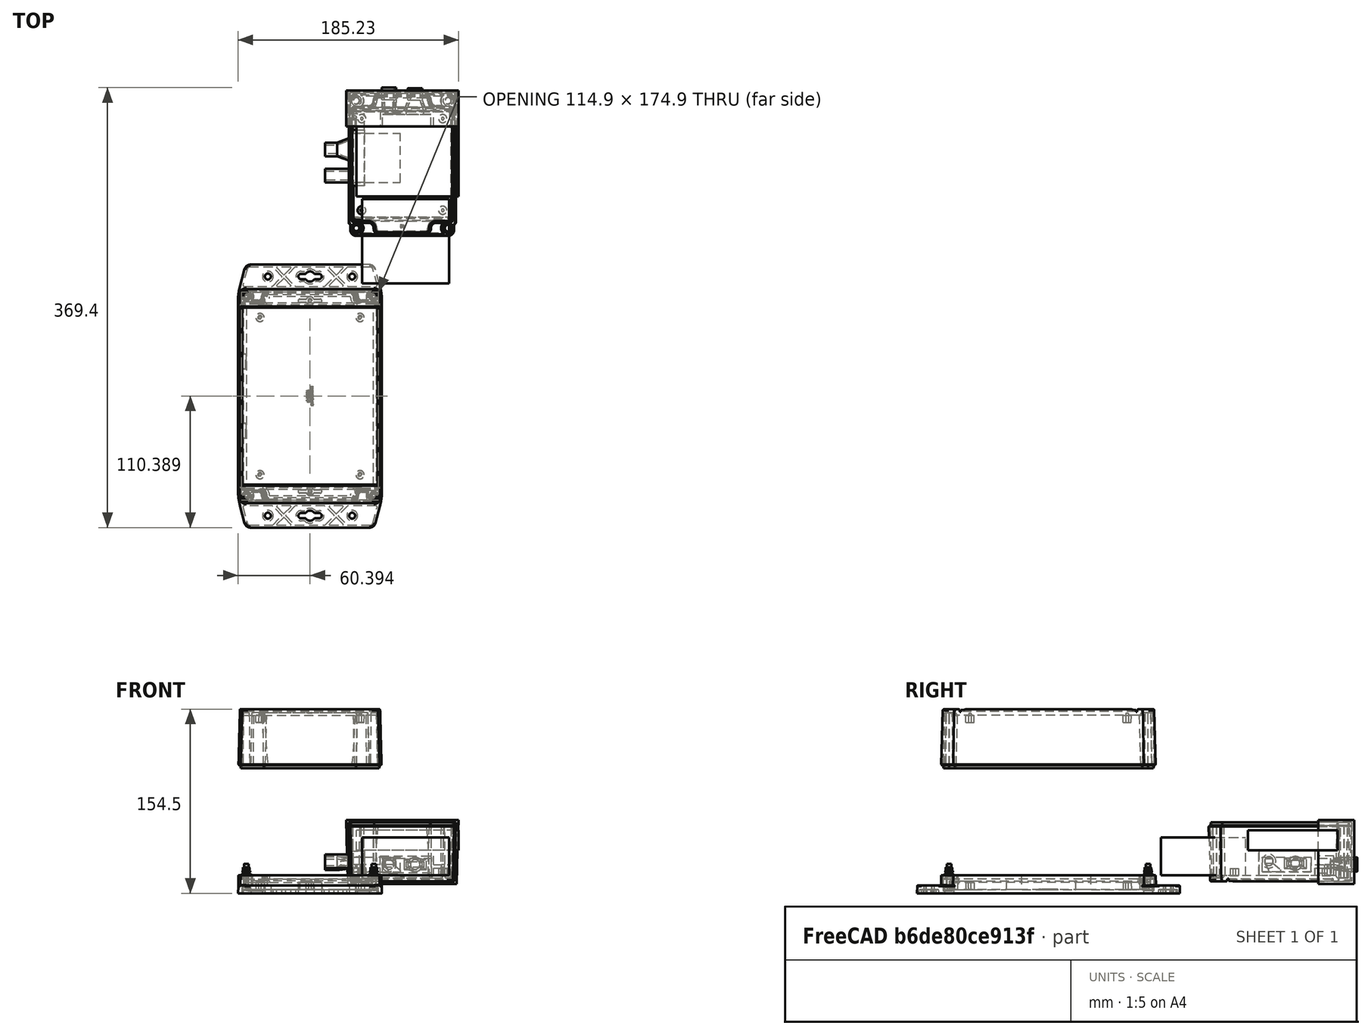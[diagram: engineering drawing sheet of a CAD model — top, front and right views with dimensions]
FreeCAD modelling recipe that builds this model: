
FCSTD DOCUMENT  (FreeCAD 0.19R24366 (Git))
Label: pzld_pm_sensor_mount
License: All rights reserved
LicenseURL: http://en.wikipedia.org/wiki/All_rights_reserved
objects: Sketcher::SketchObject×25, Part::Feature×12, PartDesign::Pad×11, PartDesign::Pocket×10, PartDesign::AdditiveLoft×3, PartDesign::Body×3, Part::Box×3, App::Part×2, PartDesign::ShapeBinder×2, TechDraw::DrawSVGTemplate×1, TechDraw::DrawViewPart×1, TechDraw::DrawViewDimension×1, TechDraw::DrawPage×1, Spreadsheet::Sheet×1
note: 93 computed .brp shape members not serialized (recipe doc carries the construction recipe); baked Part::Feature solids carry a one-line shape summary decoded from their .brp

FEATURE [Sketcher::SketchObject] Sketch  label="ref"
  FullyConstrained = false
  sketch-geometry (40):
    g0: LineSegment StartX=110.922 StartY=9.52227 StartZ=0 EndX=100.422 EndY=9.52227 EndZ=0
    g1: ArcOfCircle CenterX=110.922 CenterY=12.5223 CenterZ=0 NormalX=0 NormalY=0 NormalZ=1 AngleXU=0 Radius=3 StartAngle=4.71239 EndAngle=6.28319
    g2: LineSegment StartX=113.922 StartY=161.522 StartZ=0 EndX=113.922 EndY=12.5223 EndZ=0
    g3: ArcOfCircle CenterX=110.922 CenterY=161.522 CenterZ=0 NormalX=0 NormalY=0 NormalZ=1 AngleXU=0 Radius=3 StartAngle=0 EndAngle=1.5708
    g4: LineSegment StartX=100.422 StartY=164.522 StartZ=0 EndX=110.922 EndY=164.522 EndZ=0
    g5: LineSegment StartX=94.4224 StartY=171.022 StartZ=0 EndX=94.4224 EndY=170.522 EndZ=0
    g6: ArcOfCircle CenterX=91.4224 CenterY=171.022 CenterZ=0 NormalX=0 NormalY=0 NormalZ=1 AngleXU=0 Radius=3 StartAngle=0 EndAngle=1.5708
    g7: LineSegment StartX=22.4224 StartY=174.022 StartZ=0 EndX=91.4224 EndY=174.022 EndZ=0
    g8: ArcOfCircle CenterX=22.4224 CenterY=171.022 CenterZ=0 NormalX=0 NormalY=0 NormalZ=1 AngleXU=0 Radius=3 StartAngle=1.5708 EndAngle=3.14159
    g9: LineSegment StartX=19.4224 StartY=170.522 StartZ=0 EndX=19.4224 EndY=171.022 EndZ=0
    g10: ArcOfCircle CenterX=13.4224 CenterY=170.522 CenterZ=0 NormalX=0 NormalY=0 NormalZ=1 AngleXU=0 Radius=6 StartAngle=4.71239 EndAngle=6.28319
    g11: ArcOfCircle CenterX=100.422 CenterY=170.522 CenterZ=0 NormalX=0 NormalY=0 NormalZ=1 AngleXU=0 Radius=6 StartAngle=3.14159 EndAngle=4.71239
    g12: LineSegment StartX=2.92236 StartY=164.522 StartZ=0 EndX=13.4224 EndY=164.522 EndZ=0
    g13: ArcOfCircle CenterX=2.92236 CenterY=161.522 CenterZ=0 NormalX=0 NormalY=0 NormalZ=1 AngleXU=0 Radius=3 StartAngle=1.5708 EndAngle=3.14159
    g14: LineSegment StartX=-0.0776441 StartY=12.5223 StartZ=0 EndX=-0.0776441 EndY=161.522 EndZ=0
    g15: ArcOfCircle CenterX=2.92236 CenterY=12.5223 CenterZ=0 NormalX=0 NormalY=0 NormalZ=1 AngleXU=0 Radius=3 StartAngle=3.14159 EndAngle=4.71239
    g16: LineSegment StartX=13.4224 StartY=9.52227 StartZ=0 EndX=2.92236 EndY=9.52227 EndZ=0
    g17: ArcOfCircle CenterX=13.4224 CenterY=3.52227 CenterZ=0 NormalX=0 NormalY=0 NormalZ=1 AngleXU=0 Radius=6 StartAngle=0 EndAngle=1.5708
    g18: LineSegment StartX=19.4224 StartY=3.02227 StartZ=0 EndX=19.4224 EndY=3.52227 EndZ=0
    g19: ArcOfCircle CenterX=22.4224 CenterY=3.02227 CenterZ=0 NormalX=0 NormalY=0 NormalZ=1 AngleXU=0 Radius=3 StartAngle=3.14159 EndAngle=4.71239
    g20: LineSegment StartX=91.4224 StartY=0.0222689 StartZ=0 EndX=22.4224 EndY=0.0222689 EndZ=0
    g21: ArcOfCircle CenterX=91.4224 CenterY=3.02227 CenterZ=0 NormalX=0 NormalY=0 NormalZ=1 AngleXU=0 Radius=3 StartAngle=4.71239 EndAngle=6.28319
    g22: LineSegment StartX=94.4224 StartY=3.52227 StartZ=0 EndX=94.4224 EndY=3.02227 EndZ=0
    g23: ArcOfCircle CenterX=100.422 CenterY=3.52227 CenterZ=0 NormalX=0 NormalY=0 NormalZ=1 AngleXU=0 Radius=6 StartAngle=1.5708 EndAngle=3.14159
    g24: Circle CenterX=14.9224 CenterY=153.022 CenterZ=0 NormalX=0 NormalY=0 NormalZ=-1 AngleXU=0 Radius=1.05955
    g25: Circle CenterX=14.9224 CenterY=153.022 CenterZ=0 NormalX=0 NormalY=0 NormalZ=-1 AngleXU=0 Radius=1.125
    g26: Circle CenterX=14.9224 CenterY=153.022 CenterZ=0 NormalX=0 NormalY=0 NormalZ=-1 AngleXU=0 Radius=3.39527
    g27: Circle CenterX=98.9224 CenterY=153.022 CenterZ=0 NormalX=0 NormalY=0 NormalZ=-1 AngleXU=0 Radius=3.39527
    g28: Circle CenterX=14.9224 CenterY=21.0223 CenterZ=0 NormalX=0 NormalY=0 NormalZ=-1 AngleXU=0 Radius=3.39527
    g29: Circle CenterX=98.9224 CenterY=21.0223 CenterZ=0 NormalX=0 NormalY=0 NormalZ=-1 AngleXU=0 Radius=3.39527
    g30: Circle CenterX=98.9224 CenterY=21.0223 CenterZ=0 NormalX=0 NormalY=0 NormalZ=-1 AngleXU=0 Radius=3.5
    g31: Circle CenterX=14.9224 CenterY=21.0223 CenterZ=0 NormalX=0 NormalY=0 NormalZ=-1 AngleXU=0 Radius=3.5
    g32: Circle CenterX=14.9224 CenterY=153.022 CenterZ=0 NormalX=0 NormalY=0 NormalZ=-1 AngleXU=0 Radius=3.5
    g33: Circle CenterX=98.9224 CenterY=153.022 CenterZ=0 NormalX=0 NormalY=0 NormalZ=-1 AngleXU=0 Radius=3.5
    g34: Circle CenterX=98.9224 CenterY=153.022 CenterZ=0 NormalX=0 NormalY=0 NormalZ=-1 AngleXU=0 Radius=1.05955
    g35: Circle CenterX=98.9224 CenterY=153.022 CenterZ=0 NormalX=0 NormalY=0 NormalZ=-1 AngleXU=0 Radius=1.125
    g36: Circle CenterX=14.9224 CenterY=21.0223 CenterZ=0 NormalX=0 NormalY=0 NormalZ=-1 AngleXU=0 Radius=1.05955
    g37: Circle CenterX=14.9224 CenterY=21.0223 CenterZ=0 NormalX=0 NormalY=0 NormalZ=-1 AngleXU=0 Radius=1.125
    g38: Circle CenterX=98.9224 CenterY=21.0223 CenterZ=0 NormalX=0 NormalY=0 NormalZ=-1 AngleXU=0 Radius=1.05955
    g39: Circle CenterX=98.9224 CenterY=21.0223 CenterZ=0 NormalX=0 NormalY=0 NormalZ=-1 AngleXU=0 Radius=1.125
  constraints (2):
    c: Radius(g32) = 3.5
    c: Radius(g25) = 1.125
FEATURE [Sketcher::SketchObject] Sketch001  label="base"
  ExternalGeometry = -> [Sketch]
  FullyConstrained = true
  MapMode = 5
  Support = -> [XY_Plane]
  sketch-geometry (9):
    g0: LineSegment StartX=12.9224 StartY=140.022 StartZ=0 EndX=53.9224 EndY=140.022 EndZ=0
    g1: LineSegment StartX=53.9224 StartY=140.022 StartZ=0 EndX=53.9224 EndY=99.0223 EndZ=0
    g2: LineSegment StartX=53.9224 StartY=99.0223 StartZ=0 EndX=12.9224 EndY=99.0223 EndZ=0
    g3: LineSegment StartX=12.9224 StartY=99.0223 StartZ=0 EndX=12.9224 EndY=140.022 EndZ=0
    g4: LineSegment StartX=9.92236 StartY=143.022 StartZ=0 EndX=68.9224 EndY=143.022 EndZ=0
    g5: LineSegment StartX=68.9224 StartY=143.022 StartZ=0 EndX=68.9224 EndY=96.0223 EndZ=0
    g6: LineSegment StartX=68.9224 StartY=96.0223 StartZ=0 EndX=9.92236 EndY=96.0223 EndZ=0
    g7: LineSegment StartX=9.92236 StartY=96.0223 StartZ=0 EndX=9.92236 EndY=143.022 EndZ=0
    g8: GeomPoint X=-0.0776441 Y=96.0223 Z=0
  constraints (26):
    c: Coincident(g0,g1)
    c: Coincident(g1,g2)
    c: Coincident(g2,g3)
    c: Coincident(g3,g0)
    c: Horizontal(g0)
    c: Horizontal(g2)
    c: Vertical(g1)
    c: Vertical(g3)
    c: DistanceX(g0,g0) = 41
    c: DistanceY(g1,g1) = 41
    c: Coincident(g4,g5)
    c: Coincident(g5,g6)
    c: Coincident(g6,g7)
    c: Coincident(g7,g4)
    c: Horizontal(g4)
    c: Horizontal(g6)
    c: Vertical(g5)
    c: Vertical(g7)
    c: DistanceX(g4,g0) = 3
    c: DistanceY(g0,g4) = 3
    c: DistanceX(g0,g4) = 15
    c: DistanceY(g5,g1) = 3
    c: PointOnObject(g8,g-3)
    c: Horizontal(g8,g6)
    c: DistanceX(g8,g6) = 10
    c: DistanceY(g4,g-4) = 10
FEATURE [PartDesign::Pad] Pad
  Direction = (1,1,1)
  Length = 20.5
  Length2 = 100
  Profile = -> Sketch001
  Type = 0
FEATURE [Sketcher::SketchObject] Sketch002
  ExternalGeometry = -> [Pad]
  FullyConstrained = true
  MapMode = 5
  Placement = pos=(0,0,20.5) rot=(0,0,1;0rad)
  Support = -> [Pad]
  sketch-geometry (4):
    g0: LineSegment StartX=68.9224 StartY=143.022 StartZ=0 EndX=22.9224 EndY=143.022 EndZ=0
    g1: LineSegment StartX=22.9224 StartY=143.022 StartZ=0 EndX=22.9224 EndY=96.0223 EndZ=0
    g2: LineSegment StartX=22.9224 StartY=96.0223 StartZ=0 EndX=68.9224 EndY=96.0223 EndZ=0
    g3: LineSegment StartX=68.9224 StartY=96.0223 StartZ=0 EndX=68.9224 EndY=143.022 EndZ=0
  constraints (11):
    c: Coincident(g0,g1)
    c: Coincident(g1,g2)
    c: Coincident(g2,g3)
    c: Coincident(g3,g0)
    c: Horizontal(g0)
    c: Horizontal(g2)
    c: Vertical(g1)
    c: Vertical(g3)
    c: Coincident(g0,g-5)
    c: PointOnObject(g1,g-4)
    c: DistanceX(g-6,g0) = 13
FEATURE [PartDesign::Pocket] Pocket
  BaseFeature = -> Pad
  Length = 17.5
  Length2 = 100
  Profile = -> Sketch002
  Type = 0
FEATURE [Sketcher::SketchObject] Sketch003
  ExternalGeometry = -> [Pocket]
  FullyConstrained = true
  MapMode = 5
  Placement = pos=(22.9224,0,0) rot=(0.57735,0.57735,0.57735;2.0944rad)
  Support = -> [Pocket]
  sketch-geometry (4):
    g0: LineSegment StartX=99.0223 StartY=15.5 StartZ=0 EndX=140.022 EndY=15.5 EndZ=0
    g1: LineSegment StartX=140.022 StartY=15.5 StartZ=0 EndX=140.022 EndY=3 EndZ=0
    g2: LineSegment StartX=140.022 StartY=3 StartZ=0 EndX=99.0223 EndY=3 EndZ=0
    g3: LineSegment StartX=99.0223 StartY=3 StartZ=0 EndX=99.0223 EndY=15.5 EndZ=0
  constraints (12):
    c: Coincident(g0,g1)
    c: Coincident(g1,g2)
    c: Coincident(g2,g3)
    c: Coincident(g3,g0)
    c: Horizontal(g0)
    c: Horizontal(g2)
    c: Vertical(g1)
    c: Vertical(g3)
    c: DistanceX(g-4,g0) = 3
    c: DistanceX(g0,g-5) = 3
    c: PointOnObject(g1,g-6)
    c: DistanceY(g3,g3) = 12.5
FEATURE [PartDesign::Pocket] Pocket001
  BaseFeature = -> Pocket
  Length = 10
  Length2 = 100
  Profile = -> Sketch003
  Type = 0
FEATURE [Sketcher::SketchObject] Sketch004
  ExternalGeometry = -> [Pocket001]
  FullyConstrained = true
  MapMode = 5
  Placement = pos=(9.92236,0,0) rot=(0.57735,-0.57735,-0.57735;2.0944rad)
  Support = -> [Pocket001]
  sketch-geometry (11):
    g0: LineSegment StartX=-143.022 StartY=3 StartZ=0 EndX=-96.0223 EndY=3 EndZ=0
    g1: LineSegment StartX=-134.022 StartY=12.55 StartZ=0 EndX=-119.222 EndY=12.55 EndZ=0
    g2: LineSegment StartX=-119.222 StartY=12.55 StartZ=0 EndX=-119.222 EndY=7.8 EndZ=0
    g3: LineSegment StartX=-119.222 StartY=7.8 StartZ=0 EndX=-134.022 EndY=7.8 EndZ=0
    g4: LineSegment StartX=-134.022 StartY=7.8 StartZ=0 EndX=-134.022 EndY=12.55 EndZ=0
    g5: LineSegment StartX=-107.822 StartY=13.7 StartZ=0 EndX=-101.222 EndY=13.7 EndZ=0
    g6: LineSegment StartX=-101.222 StartY=13.7 StartZ=0 EndX=-101.222 EndY=10.2 EndZ=0
    g7: LineSegment StartX=-101.222 StartY=10.2 StartZ=0 EndX=-107.822 EndY=10.2 EndZ=0
    g8: LineSegment StartX=-107.822 StartY=10.2 StartZ=0 EndX=-107.822 EndY=13.7 EndZ=0
    g9: LineSegment StartX=-140.022 StartY=20.5 StartZ=0 EndX=-140.022 EndY=3 EndZ=0
    g10: LineSegment StartX=-99.0223 StartY=20.5 StartZ=0 EndX=-99.0223 EndY=3 EndZ=0
  constraints (36):
    c: PointOnObject(g0,g-5)
    c: PointOnObject(g0,g-4)
    c: Horizontal(g0)
    c: DistanceY(g-6,g0) = 3
    c: Coincident(g1,g2)
    c: Coincident(g2,g3)
    c: Coincident(g3,g4)
    c: Coincident(g4,g1)
    c: Horizontal(g1)
    c: Horizontal(g3)
    c: Vertical(g2)
    c: Vertical(g4)
    c: DistanceY(g0,g3) = 4.8
    c: DistanceX(g1,g1) = 14.8
    c: DistanceY(g4,g4) = 4.75
    c: Coincident(g5,g6)
    c: Coincident(g6,g7)
    c: Coincident(g7,g8)
    c: Coincident(g8,g5)
    c: Horizontal(g5)
    c: Horizontal(g7)
    c: Vertical(g6)
    c: Vertical(g8)
    c: DistanceX(g5,g5) = 6.6
    c: DistanceY(g8,g8) = 3.5
    c: PointOnObject(g9,g-3)
    c: PointOnObject(g9,g0)
    c: Vertical(g9)
    c: PointOnObject(g10,g-3)
    c: PointOnObject(g10,g0)
    c: Vertical(g10)
    c: DistanceX(g-5,g9) = 3
    c: DistanceX(g10,g-4) = 3
    c: DistanceX(g9,g1) = 6
    c: DistanceX(g5,g10) = 2.2
    c: DistanceY(g0,g6) = 7.2
FEATURE [PartDesign::Pocket] Pocket002
  BaseFeature = -> Pocket001
  Length = 5
  Length2 = 100
  Profile = -> Sketch004
  Type = 0
FEATURE [Sketcher::SketchObject] Sketch005
  ExternalGeometry = -> [Pocket002]
  FullyConstrained = true
  MapMode = 5
  Placement = pos=(12.9224,0,0) rot=(0.57735,0.57735,0.57735;2.0944rad)
  Support = -> [Pocket002]
  sketch-geometry (7):
    g0: LineSegment StartX=104.222 StartY=5 StartZ=0 EndX=114.222 EndY=5 EndZ=0
    g1: LineSegment StartX=114.222 StartY=5 StartZ=0 EndX=114.222 EndY=3 EndZ=0
    g2: LineSegment StartX=114.222 StartY=3 StartZ=0 EndX=104.222 EndY=3 EndZ=0
    g3: LineSegment StartX=104.222 StartY=3 StartZ=0 EndX=104.222 EndY=5 EndZ=0
    g4: LineSegment StartX=107.822 StartY=10.2 StartZ=0 EndX=114.222 EndY=5 EndZ=0
    g5: LineSegment StartX=104.222 StartY=5 StartZ=0 EndX=101.222 EndY=10.2 EndZ=0
    g6: LineSegment StartX=101.222 StartY=10.2 StartZ=0 EndX=107.822 EndY=10.2 EndZ=0
  constraints (18):
    c: Coincident(g0,g1)
    c: Coincident(g1,g2)
    c: Coincident(g2,g3)
    c: Coincident(g3,g0)
    c: Horizontal(g0)
    c: Horizontal(g2)
    c: Vertical(g1)
    c: Vertical(g3)
    c: DistanceX(g0,g0) = 10
    c: DistanceY(g1,g1) = 2
    c: DistanceX(g-4,g2) = 5.2
    c: PointOnObject(g2,g-5)
    c: Coincident(g4,g-3)
    c: Coincident(g4,g0)
    c: Coincident(g5,g0)
    c: Coincident(g5,g-3)
    c: Coincident(g6,g5)
    c: Coincident(g6,g4)
FEATURE [PartDesign::Pocket] Pocket003
  BaseFeature = -> Pocket002
  Length = 1.5
  Length2 = 100
  Profile = -> Sketch005
  Type = 0
FEATURE [Sketcher::SketchObject] Sketch006
  ExternalGeometry = -> [Pocket003]
  FullyConstrained = true
  MapMode = 5
  Placement = pos=(9.92236,0,0) rot=(0.57735,-0.57735,-0.57735;2.0944rad)
  Support = -> [Pocket003]
  sketch-geometry (6):
    g0: LineSegment StartX=-107.822 StartY=10.2 StartZ=0 EndX=-101.222 EndY=13.7 EndZ=0
    g1: LineSegment StartX=-107.822 StartY=13.7 StartZ=0 EndX=-101.222 EndY=10.2 EndZ=0
    g2: GeomPoint X=-104.522 Y=11.95 Z=0
    g3: Circle CenterX=-104.522 CenterY=11.95 CenterZ=0 NormalX=0 NormalY=0 NormalZ=1 AngleXU=0 Radius=3.7353
    g4: Circle CenterX=-104.522 CenterY=11.95 CenterZ=0 NormalX=0 NormalY=0 NormalZ=1 AngleXU=0 Radius=5.7353
    g5: LineSegment StartX=-100.787 StartY=11.95 StartZ=0 EndX=-98.787 EndY=11.95 EndZ=0
  constraints (14):
    c: Coincident(g0,g-3)
    c: Coincident(g0,g-5)
    c: Coincident(g1,g-4)
    c: Coincident(g1,g-6)
    c: PointOnObject(g2,g0)
    c: PointOnObject(g2,g1)
    c: Coincident(g3,g2)
    c: PointOnObject(g0,g3)
    c: Coincident(g4,g3)
    c: PointOnObject(g5,g3)
    c: PointOnObject(g5,g4)
    c: Horizontal(g5)
    c: Perpendicular(g3,g5)
    c: DistanceX(g5,g5) = 2
FEATURE [PartDesign::Pad] Pad001
  BaseFeature = -> Pocket003
  Direction = (1,1,1)
  Length = 20
  Length2 = 100
  Profile = -> Sketch006
  Type = 0
FEATURE [Sketcher::SketchObject] Sketch007
  ExternalGeometry = -> [Pad001]
  FullyConstrained = true
  MapMode = 5
  Placement = pos=(9.92236,0,0) rot=(0.57735,-0.57735,-0.57735;2.0944rad)
  Support = -> [Pad001]
  sketch-geometry (8):
    g0: LineSegment StartX=-134.022 StartY=12.55 StartZ=0 EndX=-119.222 EndY=12.55 EndZ=0
    g1: LineSegment StartX=-119.222 StartY=12.55 StartZ=0 EndX=-119.222 EndY=7.8 EndZ=0
    g2: LineSegment StartX=-119.222 StartY=7.8 StartZ=0 EndX=-134.022 EndY=7.8 EndZ=0
    g3: LineSegment StartX=-134.022 StartY=7.8 StartZ=0 EndX=-134.022 EndY=12.55 EndZ=0
    g4: LineSegment StartX=-136.022 StartY=14.55 StartZ=0 EndX=-117.222 EndY=14.55 EndZ=0
    g5: LineSegment StartX=-117.222 StartY=14.55 StartZ=0 EndX=-117.222 EndY=5.8 EndZ=0
    g6: LineSegment StartX=-117.222 StartY=5.8 StartZ=0 EndX=-136.022 EndY=5.8 EndZ=0
    g7: LineSegment StartX=-136.022 StartY=5.8 StartZ=0 EndX=-136.022 EndY=14.55 EndZ=0
  constraints (22):
    c: Coincident(g0,g1)
    c: Coincident(g1,g2)
    c: Coincident(g2,g3)
    c: Coincident(g3,g0)
    c: Horizontal(g0)
    c: Horizontal(g2)
    c: Vertical(g1)
    c: Vertical(g3)
    c: Coincident(g0,g-3)
    c: Coincident(g1,g-4)
    c: Coincident(g4,g5)
    c: Coincident(g5,g6)
    c: Coincident(g6,g7)
    c: Coincident(g7,g4)
    c: Horizontal(g4)
    c: Horizontal(g6)
    c: Vertical(g5)
    c: Vertical(g7)
    c: DistanceY(g0,g4) = 2
    c: DistanceX(g4,g0) = 2
    c: DistanceX(g1,g5) = 2
    c: DistanceY(g5,g1) = 2
FEATURE [Sketcher::SketchObject] Sketch008
  AttachmentOffset = pos=(0,7,10) rot=(0,0,1;0rad)
  ExternalGeometry = -> [Pad001]
  FullyConstrained = true
  MapMode = 5
  Placement = pos=(-0.0776441,0,7) rot=(0.57735,-0.57735,-0.57735;2.0944rad)
  Support = -> [Pad001]
  sketch-geometry (6):
    g0: LineSegment StartX=-134.022 StartY=5.55 StartZ=0 EndX=-119.222 EndY=0.8 EndZ=0
    g1: LineSegment StartX=-119.222 StartY=5.55 StartZ=0 EndX=-134.022 EndY=0.8 EndZ=0
    g2: GeomPoint X=-126.622 Y=3.175 Z=0
    g3: Circle CenterX=-126.622 CenterY=3.175 CenterZ=0 NormalX=0 NormalY=0 NormalZ=1 AngleXU=0 Radius=3.73
    g4: Circle CenterX=-126.622 CenterY=3.175 CenterZ=0 NormalX=0 NormalY=0 NormalZ=1 AngleXU=0 Radius=5.73
    g5: LineSegment StartX=-122.892 StartY=3.175 StartZ=0 EndX=-120.892 EndY=3.175 EndZ=0
  constraints (14):
    c: Coincident(g0,g-3)
    c: Coincident(g0,g-4)
    c: Coincident(g1,g-5)
    c: Coincident(g1,g-6)
    c: PointOnObject(g2,g1)
    c: PointOnObject(g2,g0)
    c: Coincident(g3,g2)
    c: Coincident(g4,g3)
    c: PointOnObject(g5,g3)
    c: PointOnObject(g5,g4)
    c: Horizontal(g5)
    c: Perpendicular(g3,g5)
    c: DistanceX(g5,g5) = 2
    c: Radius(g3) = 3.73
FEATURE [PartDesign::AdditiveLoft] AdditiveLoft
  BaseFeature = -> Pad001
  Closed = false
  Profile = -> Sketch007
  Ruled = false
  Sections = -> [Sketch008]
FEATURE [PartDesign::Pad] Pad002
  BaseFeature = -> AdditiveLoft
  Direction = (1,1,1)
  Length = 10
  Length2 = 100
  Profile = -> AdditiveLoft [Face22]
  Type = 0
FEATURE [Sketcher::SketchObject] Sketch009
  ExternalGeometry = -> [Pad002]
  FullyConstrained = true
  MapMode = 5
  Placement = pos=(0,143.022,0) rot=(0,0.707107,0.707107;3.14159rad)
  Support = -> [Pad002]
  sketch-geometry (5):
    g0: GeomPoint X=-9.92236 Y=6 Z=0
    g1: LineSegment StartX=-9.92236 StartY=6 StartZ=0 EndX=-22.9224 EndY=6 EndZ=0
    g2: LineSegment StartX=-22.9224 StartY=6 StartZ=0 EndX=-22.9224 EndY=9 EndZ=0
    g3: LineSegment StartX=-22.9224 StartY=9 StartZ=0 EndX=-9.92236 EndY=9 EndZ=0
    g4: LineSegment StartX=-9.92236 StartY=9 StartZ=0 EndX=-9.92236 EndY=6 EndZ=0
  constraints (13):
    c: PointOnObject(g0,g-4)
    c: DistanceY(g-4,g0) = 6
    c: Coincident(g1,g2)
    c: Coincident(g2,g3)
    c: Coincident(g3,g4)
    c: Coincident(g4,g1)
    c: Horizontal(g1)
    c: Horizontal(g3)
    c: Vertical(g2)
    c: Vertical(g4)
    c: Coincident(g1,g0)
    c: PointOnObject(g2,g-5)
    c: DistanceY(g2,g2) = 3
FEATURE [PartDesign::Pad] Pad003
  BaseFeature = -> Pad002
  Direction = (1,1,1)
  Length = 13.5
  Length2 = 100
  Profile = -> Sketch009
  Type = 0
FEATURE [Sketcher::SketchObject] Sketch010
  ExternalGeometry = -> [Pad003]
  FullyConstrained = true
  MapMode = 5
  Placement = pos=(0,2e-15,9) rot=(0,0,1;0rad)
  Support = -> [Pad003]
  sketch-geometry (3):
    g0: Circle CenterX=14.9224 CenterY=153.022 CenterZ=0 NormalX=0 NormalY=0 NormalZ=-1 AngleXU=0 Radius=1.125
    g1: Circle CenterX=14.9224 CenterY=153.022 CenterZ=0 NormalX=0 NormalY=0 NormalZ=1 AngleXU=0 Radius=1.625
    g2: LineSegment StartX=13.2974 StartY=153.022 StartZ=0 EndX=13.7974 EndY=153.022 EndZ=0
  constraints (9):
    c: Radius(g0) = 1.125
    c: Coincident(g1,g0)
    c: PointOnObject(g2,g1)
    c: PointOnObject(g2,g0)
    c: Horizontal(g2)
    c: Perpendicular(g0,g2)
    c: DistanceY(g1,g-3) = 3.5
    c: DistanceX(g-3,g1) = 5
    c: DistanceX(g2,g2) = 0.5
FEATURE [PartDesign::Pocket] Pocket004
  BaseFeature = -> Pad003
  Length = 5
  Length2 = 100
  Profile = -> Sketch010
  Type = 2
FEATURE [Sketcher::SketchObject] Sketch011
  ExternalGeometry = -> [Pocket004]
  FullyConstrained = true
  MapMode = 5
  Placement = pos=(0,0,3) rot=(0,0,1;0rad)
  Support = -> [Pocket004]
  sketch-geometry (4):
    g0: LineSegment StartX=68.9224 StartY=143.022 StartZ=0 EndX=22.9224 EndY=143.022 EndZ=0
    g1: LineSegment StartX=22.9224 StartY=143.022 StartZ=0 EndX=22.9224 EndY=96.0223 EndZ=0
    g2: LineSegment StartX=22.9224 StartY=96.0223 StartZ=0 EndX=68.9224 EndY=96.0223 EndZ=0
    g3: LineSegment StartX=68.9224 StartY=96.0223 StartZ=0 EndX=68.9224 EndY=143.022 EndZ=0
  constraints (10):
    c: Coincident(g0,g1)
    c: Coincident(g1,g2)
    c: Coincident(g2,g3)
    c: Coincident(g3,g0)
    c: Horizontal(g0)
    c: Horizontal(g2)
    c: Vertical(g1)
    c: Vertical(g3)
    c: Coincident(g0,g-4)
    c: Coincident(g1,g-5)
FEATURE [PartDesign::Pocket] Pocket005
  BaseFeature = -> Pocket004
  Length = 5
  Length2 = 100
  Profile = -> Sketch011
  Type = 0
FEATURE [PartDesign::Body] Body  label="Mount V1"
  Group = -> [Sketch001,Sketch,Pad,Sketch002,Pocket,Sketch003,Pocket001,Sketch004,Pocket002,Sketch005,Pocket003,Sketch006,Pad001,Sketch007,Sketch008,AdditiveLoft,Pad002,Sketch009,Pad003,Sketch010,Pocket004,Sketch011,Pocket005]
  Origin = -> Origin
  Placement = pos=(-1,0,0) rot=(0,0,1;0rad)
  Tip = -> Pocket005
FEATURE [TechDraw::DrawSVGTemplate] Template
  EditableTexts = Designed_by_Name=Designed by Name; Drawing_number=Drawing number; FC-Date=Date; FC-SC=Scale; FC-SH=Sheet; FC-Title=Title; Subtitle=Subtitle; Weight=Weight
  Height = 210
  Orientation = 1
  Width = 297
FEATURE [TechDraw::DrawViewPart] View
  CoarseView = false
  Direction = (-1,0,0)
  Focus = 100
  HardHidden = false
  IsoCount = 0
  IsoHidden = false
  IsoVisible = false
  LockPosition = false
  Perspective = false
  Rotation = 0
  ScaleType = 0
  SeamHidden = false
  SeamVisible = true
  SmoothHidden = false
  SmoothVisible = true
  Source = -> [Body]
  X = 140.834
  XDirection = (0,-1,0)
  Y = 104.313
FEATURE [TechDraw::DrawViewDimension] Dimension
  Arbitrary = false
  ArbitraryTolerances = false
  EqualTolerance = true
  FormatSpec = %.2f
  FormatSpecOverTolerance = %+.2f
  FormatSpecUnderTolerance = %+.2f
  Inverted = false
  LockPosition = false
  MeasureType = 1
  OverTolerance = 0
  References2D = -> [View]
  Rotation = 0
  ScaleType = 0
  TheoreticalExact = false
  Type = 2
  UnderTolerance = 0
  X = -48.3191
  Y = 14.3169
FEATURE [TechDraw::DrawPage] Page
  KeepUpdated = true
  NextBalloonIndex = 1
  ProjectionType = 0
  Template = -> Template
  Views = -> [View,Dimension]
FEATURE [Part::Feature] Part__Feature  label="1555HF LID"
  Placement = pos=(0,0,0) rot=(0,0,-1;1.5708rad)
  shape: bbox 120.8 x 220.8 x 504.2 mm, 858 faces (baked)
FEATURE [Part::Feature] Part__Feature001  label="1555HF42 BOX"
  Placement = pos=(-71.7099,-3.23523,92.5) rot=(0.707107,-0.707107,0;3.14159rad)
  shape: bbox 120 x 180 x 443.8 mm, 283 faces (baked)
FEATURE [Part::Feature] Part__Feature002  label="1555HF Panel"
  Placement = pos=(-23.8365,-80.5112,-4.5522) rot=(0.707107,-0.707107,0;3.14159rad)
  shape: bbox 106.7 x 167.1 x 1.448 mm, 20 faces (baked)
FEATURE [Part::Feature] Part__Feature003  label="SC576 (screw M4-0.7X 20mm PN)"
  Placement = pos=(-77.3365,2.98878,-10) rot=(-1,0,0;1.5708rad)
  shape: bbox 7.373 x 7.373 x 22.24 mm, 29 faces (baked)
FEATURE [Part::Feature] Part__Feature004  label="SC576 (screw M4-0.7X 20mm PN)001"
  Placement = pos=(29.6635,2.98878,-10) rot=(-1,0,0;1.5708rad)
  shape: bbox 7.373 x 7.373 x 22.24 mm, 29 faces (baked)
FEATURE [Part::Feature] Part__Feature005  label="SC576 (screw M4-0.7X 20mm PN)002"
  Placement = pos=(29.6635,-164.011,-10) rot=(-1,0,0;1.5708rad)
  shape: bbox 7.373 x 7.373 x 22.24 mm, 29 faces (baked)
FEATURE [Part::Feature] Part__Feature006  label="SC576 (screw M4-0.7X 20mm PN)003"
  Placement = pos=(-77.3365,-164.011,-10) rot=(-1,0,0;1.5708rad)
  shape: bbox 7.373 x 7.373 x 22.24 mm, 29 faces (baked)
FEATURE [Part::Feature] Part__Feature007  label="IN-M4 (insert M4-0.7X5.75mm SS)"
  Placement = pos=(29.6635,2.98878,6.85) rot=(-1,0,0;1.5708rad)
  shape: bbox 6.35 x 6.35 x 6.35 mm, 16 faces (baked)
FEATURE [Part::Feature] Part__Feature008  label="IN-M4 (insert M4-0.7X5.75mm SS)001"
  Placement = pos=(-77.3365,-164.011,6.85) rot=(-1,0,0;1.5708rad)
  shape: bbox 6.35 x 6.35 x 6.35 mm, 16 faces (baked)
FEATURE [Part::Feature] Part__Feature009  label="IN-M4 (insert M4-0.7X5.75mm SS)002"
  Placement = pos=(-77.3365,2.98878,6.85) rot=(-1,0,0;1.5708rad)
  shape: bbox 6.35 x 6.35 x 6.35 mm, 16 faces (baked)
FEATURE [Part::Feature] Part__Feature010  label="IN-M4 (insert M4-0.7X5.75mm SS)003"
  Placement = pos=(29.6635,-164.011,6.85) rot=(-1,0,0;1.5708rad)
  shape: bbox 6.35 x 6.35 x 6.35 mm, 16 faces (baked)
FEATURE [App::Part] _555HF42  label="1555HF42"
  Group = -> [Part__Feature,Part__Feature001,Part__Feature002,Part__Feature003,Part__Feature004,Part__Feature005,Part__Feature006,Part__Feature007,Part__Feature008,Part__Feature009,Part__Feature010]
  Origin = -> Origin001
  Placement = pos=(80,6,133) rot=(1,0,0;3.14159rad)
FEATURE [Part::Box] Box  label="SPS30"
  AttacherType = Attacher::AttachEngine3D
  Height = 12.5
  Length = 41
  Placement = pos=(11,99,3) rot=(0,0,1;0rad)
  Width = 41
FEATURE [Part::Box] Box001  label="Batt"
  AttacherType = Attacher::AttachEngine3D
  Height = 32
  Length = 73
  Placement = pos=(20,14,0) rot=(0,0,1;0rad)
  Width = 71
FEATURE [Part::Box] Box002  label="PCB"
  AttacherType = Attacher::AttachEngine3D
  Height = 17
  Length = 75
  Placement = pos=(101,87,21) rot=(0,0,1;1.5708rad)
  Width = 86
FEATURE [Sketcher::SketchObject] Sketch012
  FullyConstrained = true
  MapMode = 5
  Support = -> [XY_Plane002]
  expr: Constraints[10] = Spreadsheet.D4
  expr: Constraints[9] = Spreadsheet.D2
  sketch-geometry (4):
    g0: LineSegment StartX=0 StartY=0 StartZ=0 EndX=44.8 EndY=0 EndZ=0
    g1: LineSegment StartX=44.8 StartY=0 StartZ=0 EndX=44.8 EndY=13 EndZ=0
    g2: LineSegment StartX=44.8 StartY=13 StartZ=0 EndX=0 EndY=13 EndZ=0
    g3: LineSegment StartX=0 StartY=13 StartZ=0 EndX=0 EndY=0 EndZ=0
  constraints (11):
    c: Coincident(g0,g1)
    c: Coincident(g1,g2)
    c: Coincident(g2,g3)
    c: Coincident(g3,g0)
    c: Horizontal(g0)
    c: Horizontal(g2)
    c: Vertical(g1)
    c: Vertical(g3)
    c: Coincident(g0,g-1)
    c: DistanceX(g2,g2) = 44.8
    c: DistanceY(g3,g3) = 13
FEATURE [Spreadsheet::Sheet] Spreadsheet  label="dimensions"
  cells = B1=original; C1=padding; D1=total; A2=front_width; B2=40.8; C2=2; D2==B2 + C2 * 2; A3=front_height; B3=12.3; C3=2; D3==B3 + C3 * 2; A4=depth; B4=10; C4=3; D4==B4 + C4; A6=case_width; B6=83; A7=case_mount_p2p; B7=68; A8=wing_length; B8==(B6 - D2) / 2; C8=-1; D8==B8 + C8 * 2; A9=wing_offset; C9=3.8; A10=wing_point; B10==(B7 - D2) / 2; A11=case_screw_dia; B11=2.25; A13=space_to_start_notch; B13=2.5; A14=snout_transition_len; B14=9.5; C14=-0.5; D14==B14 + C14; A15=sbout_extension_len; B15=10; A17=pocket_margins; B17=0
FEATURE [PartDesign::Pad] Pad004  label="Base"
  Direction = (1,1,1)
  Length = 16.3
  Length2 = 100
  Profile = -> Sketch012
  Type = 0
  expr: Length = Spreadsheet.D3
FEATURE [Sketcher::SketchObject] Sketch013
  ExternalGeometry = -> [Pad004]
  FullyConstrained = true
  MapMode = 5
  Placement = pos=(0,0,0) rot=(1,0,0;1.5708rad)
  Support = -> [Pad004]
  expr: Constraints[11] = Spreadsheet.B3 + Spreadsheet.B17
  expr: Constraints[10] = Spreadsheet.B2 + Spreadsheet.B17
  sketch-geometry (5):
    g0: LineSegment StartX=2 StartY=14.3 StartZ=0 EndX=42.8 EndY=14.3 EndZ=0
    g1: LineSegment StartX=42.8 StartY=14.3 StartZ=0 EndX=42.8 EndY=2 EndZ=0
    g2: LineSegment StartX=42.8 StartY=2 StartZ=0 EndX=2 EndY=2 EndZ=0
    g3: LineSegment StartX=2 StartY=2 StartZ=0 EndX=2 EndY=14.3 EndZ=0
    g4: GeomPoint X=22.4 Y=8.15 Z=0
  constraints (12):
    c: Coincident(g0,g1)
    c: Coincident(g1,g2)
    c: Coincident(g2,g3)
    c: Coincident(g3,g0)
    c: Horizontal(g0)
    c: Horizontal(g2)
    c: Vertical(g1)
    c: Vertical(g3)
    c: Symmetric(g0,g1,g4)
    c: Symmetric(g-3,g-4,g4)
    c: DistanceX(g0,g0) = 40.8
    c: DistanceY(g3,g3) = 12.3
FEATURE [PartDesign::Pocket] Pocket006  label="Sensor pocket"
  BaseFeature = -> Pad004
  Length = 10
  Length2 = 100
  Profile = -> Sketch013
  Type = 0
  expr: Length = Spreadsheet.B4
FEATURE [Sketcher::SketchObject] Sketch014
  ExternalGeometry = -> [Pocket006]
  FullyConstrained = true
  MapMode = 5
  Placement = pos=(0,10,-2.2e-15) rot=(1,0,0;1.5708rad)
  Support = -> [Pocket006]
  sketch-geometry (8):
    g0: LineSegment StartX=4.2 StartY=12.7 StartZ=0 EndX=10.8 EndY=12.7 EndZ=0
    g1: LineSegment StartX=10.8 StartY=12.7 StartZ=0 EndX=10.8 EndY=9.2 EndZ=0
    g2: LineSegment StartX=10.8 StartY=9.2 StartZ=0 EndX=4.2 EndY=9.2 EndZ=0
    g3: LineSegment StartX=4.2 StartY=9.2 StartZ=0 EndX=4.2 EndY=12.7 EndZ=0
    g4: LineSegment StartX=22 StartY=11.55 StartZ=0 EndX=36.8 EndY=11.55 EndZ=0
    g5: LineSegment StartX=36.8 StartY=11.55 StartZ=0 EndX=36.8 EndY=6.8 EndZ=0
    g6: LineSegment StartX=36.8 StartY=6.8 StartZ=0 EndX=22 EndY=6.8 EndZ=0
    g7: LineSegment StartX=22 StartY=6.8 StartZ=0 EndX=22 EndY=11.55 EndZ=0
  constraints (24):
    c: Coincident(g0,g1)
    c: Coincident(g1,g2)
    c: Coincident(g2,g3)
    c: Coincident(g3,g0)
    c: Horizontal(g0)
    c: Horizontal(g2)
    c: Vertical(g1)
    c: Vertical(g3)
    c: Coincident(g4,g5)
    c: Coincident(g5,g6)
    c: Coincident(g6,g7)
    c: Coincident(g7,g4)
    c: Horizontal(g4)
    c: Horizontal(g6)
    c: Vertical(g5)
    c: Vertical(g7)
    c: DistanceX(g0,g0) = 6.6
    c: DistanceX(g4,g4) = 14.8
    c: DistanceY(g7,g7) = 4.75
    c: DistanceX(g-6,g0) = 2.2
    c: DistanceY(g-6,g2) = 7.2
    c: DistanceY(g3,g3) = 3.5
    c: DistanceY(g-5,g5) = 4.8
    c: DistanceX(g4,g-4) = 6
FEATURE [PartDesign::Pocket] Pocket007  label="Inlet Outlet holes"
  BaseFeature = -> Pocket006
  Length = 5
  Length2 = 100
  Profile = -> Sketch014
  Type = 2
FEATURE [Sketcher::SketchObject] Sketch015
  ExternalGeometry = -> [Pocket007]
  FullyConstrained = true
  MapMode = 5
  Placement = pos=(0,10,-2.2e-15) rot=(1,0,0;1.5708rad)
  Support = -> [Pocket007]
  sketch-geometry (6):
    g0: LineSegment StartX=7.2 StartY=2 StartZ=0 EndX=17.2 EndY=2 EndZ=0
    g1: LineSegment StartX=17.2 StartY=2 StartZ=0 EndX=17.2 EndY=4 EndZ=0
    g2: LineSegment StartX=17.2 StartY=4 StartZ=0 EndX=10.8 EndY=9.2 EndZ=0
    g3: LineSegment StartX=7.2 StartY=2 StartZ=0 EndX=7.2 EndY=4 EndZ=0
    g4: LineSegment StartX=7.2 StartY=4 StartZ=0 EndX=4.2 EndY=9.2 EndZ=0
    g5: LineSegment StartX=4.2 StartY=9.2 StartZ=0 EndX=10.8 EndY=9.2 EndZ=0
  constraints (16):
    c: PointOnObject(g0,g-3)
    c: PointOnObject(g0,g-3)
    c: DistanceX(g-3,g0) = 5.2
    c: Coincident(g2,g1)
    c: Coincident(g2,g-4)
    c: Coincident(g4,g3)
    c: Coincident(g4,g-4)
    c: DistanceX(g0,g0) = 10
    c: DistanceY(g1,g1) = 2
    c: Equal(g3,g1)
    c: Coincident(g3,g0)
    c: Coincident(g1,g0)
    c: Coincident(g5,g4)
    c: Coincident(g5,g2)
    c: Vertical(g3)
    c: Vertical(g1)
FEATURE [PartDesign::Pocket] Pocket008  label="Second inlet"
  BaseFeature = -> Pocket007
  Length = 1
  Length2 = 100
  Profile = -> Sketch015
  Type = 0
FEATURE [Sketcher::SketchObject] Sketch016
  ExternalGeometry = -> [Pocket008]
  FullyConstrained = true
  MapMode = 5
  Placement = pos=(0,0,0) rot=(0.57735,-0.57735,-0.57735;2.0944rad)
  Support = -> [Pocket008]
  sketch-geometry (4):
    g0: LineSegment StartX=-13 StartY=9 StartZ=0 EndX=0 EndY=9 EndZ=0
    g1: LineSegment StartX=0 StartY=9 StartZ=0 EndX=0 EndY=6 EndZ=0
    g2: LineSegment StartX=0 StartY=6 StartZ=0 EndX=-13 EndY=6 EndZ=0
    g3: LineSegment StartX=-13 StartY=6 StartZ=0 EndX=-13 EndY=9 EndZ=0
  constraints (12):
    c: Coincident(g0,g1)
    c: Coincident(g1,g2)
    c: Coincident(g2,g3)
    c: Coincident(g3,g0)
    c: Horizontal(g0)
    c: Horizontal(g2)
    c: Vertical(g1)
    c: Vertical(g3)
    c: Vertical(g2,g-3)
    c: Vertical(g1,g-1)
    c: DistanceY(g-3,g2) = 6
    c: DistanceY(g3,g3) = 3
FEATURE [PartDesign::Pad] Pad005  label="Wing left"
  BaseFeature = -> Pocket008
  Direction = (1,1,1)
  Length = 20.9
  Length2 = 100
  Profile = -> Sketch016
  Type = 0
  expr: Length = Spreadsheet.D8 + Spreadsheet.C9
FEATURE [Sketcher::SketchObject] Sketch017
  ExternalGeometry = -> [Pad005]
  FullyConstrained = true
  MapMode = 5
  Placement = pos=(44.8,0,0) rot=(0.57735,0.57735,0.57735;2.0944rad)
  Support = -> [Pad005]
  sketch-geometry (4):
    g0: LineSegment StartX=0 StartY=9 StartZ=0 EndX=13 EndY=9 EndZ=0
    g1: LineSegment StartX=13 StartY=9 StartZ=0 EndX=13 EndY=6 EndZ=0
    g2: LineSegment StartX=13 StartY=6 StartZ=0 EndX=0 EndY=6 EndZ=0
    g3: LineSegment StartX=0 StartY=6 StartZ=0 EndX=0 EndY=9 EndZ=0
  constraints (12):
    c: Coincident(g0,g1)
    c: Coincident(g1,g2)
    c: Coincident(g2,g3)
    c: Coincident(g3,g0)
    c: Horizontal(g0)
    c: Horizontal(g2)
    c: Vertical(g1)
    c: Vertical(g3)
    c: Vertical(g2,g-1)
    c: Vertical(g1,g-3)
    c: DistanceY(g-1,g2) = 6
    c: DistanceY(g3,g3) = 3
FEATURE [PartDesign::Pad] Pad006  label="Wing right"
  BaseFeature = -> Pad005
  Direction = (1,1,1)
  Length = 13.3
  Length2 = 100
  Profile = -> Sketch017
  Type = 0
  expr: Length = Spreadsheet.D8 - Spreadsheet.C9
FEATURE [Sketcher::SketchObject] Sketch018
  ExternalGeometry = -> [Pad006]
  FullyConstrained = true
  MapMode = 5
  Placement = pos=(0,0,9) rot=(0,0,1;0rad)
  Support = -> [Pad006]
  expr: Constraints[7] = Spreadsheet.B10 - Spreadsheet.C9
  expr: Constraints[6] = Spreadsheet.B10 + Spreadsheet.C9
  expr: Constraints[5] = Spreadsheet.B11
  sketch-geometry (4):
    g0: GeomPoint X=-20.9 Y=6.5 Z=0
    g1: GeomPoint X=58.1 Y=6.5 Z=0
    g2: Circle CenterX=-15.4 CenterY=6.5 CenterZ=0 NormalX=0 NormalY=0 NormalZ=1 AngleXU=0 Radius=1.125
    g3: Circle CenterX=52.6 CenterY=6.5 CenterZ=0 NormalX=0 NormalY=0 NormalZ=1 AngleXU=0 Radius=1.125
  constraints (8):
    c: Symmetric(g-3,g-3,g0)
    c: Symmetric(g-4,g-4,g1)
    c: Horizontal(g0,g2)
    c: Horizontal(g1,g3)
    c: Equal(g2,g3)
    c: Diameter(g2) = 2.25
    c: DistanceX(g2,g-6) = 15.4
    c: DistanceX(g-5,g3) = 7.8
FEATURE [PartDesign::Pocket] Pocket009  label="Pillar screw holes"
  BaseFeature = -> Pad006
  Length = 5
  Length2 = 100
  Profile = -> Sketch018
  Type = 2
FEATURE [Sketcher::SketchObject] Sketch019
  AttachmentOffset = pos=(0,0,9) rot=(0,0,1;0rad)
  ExternalGeometry = -> [Pocket009]
  FullyConstrained = true
  MapMode = 5
  Placement = pos=(0,22,-2e-15) rot=(0,0.707107,0.707107;3.14159rad)
  Support = -> [Pocket009]
  expr: .AttachmentOffset.Base.z = Spreadsheet.D14
  sketch-geometry (3):
    g0: Circle CenterX=-29.4 CenterY=9.175 CenterZ=0 NormalX=0 NormalY=0 NormalZ=1 AngleXU=0 Radius=4
    g1: Circle CenterX=-29.4 CenterY=9.175 CenterZ=0 NormalX=0 NormalY=0 NormalZ=1 AngleXU=0 Radius=6
    g2: GeomPoint X=-29.4 Y=9.175 Z=0
  constraints (5):
    c: Diameter(g0) = 8
    c: Coincident(g1,g0)
    c: Diameter(g1) = 12
    c: Symmetric(g-3,g-4,g2)
    c: Coincident(g0,g2)
FEATURE [Sketcher::SketchObject] Sketch020
  ExternalGeometry = -> [Pocket009]
  FullyConstrained = true
  MapMode = 5
  Placement = pos=(0,13,0) rot=(0,0.707107,0.707107;3.14159rad)
  Support = -> [Pocket009]
  sketch-geometry (9):
    g0: LineSegment StartX=-36.8 StartY=11.55 StartZ=0 EndX=-22 EndY=11.55 EndZ=0
    g1: LineSegment StartX=-22 StartY=11.55 StartZ=0 EndX=-22 EndY=6.8 EndZ=0
    g2: LineSegment StartX=-22 StartY=6.8 StartZ=0 EndX=-36.8 EndY=6.8 EndZ=0
    g3: LineSegment StartX=-36.8 StartY=6.8 StartZ=0 EndX=-36.8 EndY=11.55 EndZ=0
    g4: LineSegment StartX=-38.8 StartY=13.55 StartZ=0 EndX=-20 EndY=13.55 EndZ=0
    g5: LineSegment StartX=-20 StartY=13.55 StartZ=0 EndX=-20 EndY=4.8 EndZ=0
    g6: LineSegment StartX=-20 StartY=4.8 StartZ=0 EndX=-38.8 EndY=4.8 EndZ=0
    g7: LineSegment StartX=-38.8 StartY=4.8 StartZ=0 EndX=-38.8 EndY=13.55 EndZ=0
    g8: GeomPoint X=-29.4 Y=9.175 Z=0
  constraints (22):
    c: Coincident(g0,g1)
    c: Coincident(g1,g2)
    c: Coincident(g2,g3)
    c: Coincident(g3,g0)
    c: Horizontal(g0)
    c: Horizontal(g2)
    c: Vertical(g1)
    c: Vertical(g3)
    c: Coincident(g0,g-3)
    c: Coincident(g1,g-4)
    c: Coincident(g4,g5)
    c: Coincident(g5,g6)
    c: Coincident(g6,g7)
    c: Coincident(g7,g4)
    c: Horizontal(g4)
    c: Horizontal(g6)
    c: Vertical(g5)
    c: Vertical(g7)
    c: Symmetric(g0,g1,g8)
    c: Symmetric(g4,g5,g8)
    c: DistanceY(g0,g4) = 2
    c: DistanceX(g4,g0) = 2
FEATURE [PartDesign::AdditiveLoft] AdditiveLoft001  label="Outlet snout transition"
  BaseFeature = -> Pocket009
  Closed = false
  Profile = -> Sketch020
  Ruled = false
  Sections = -> [Sketch019]
FEATURE [PartDesign::Pad] Pad007  label="Outlet snout extension"
  BaseFeature = -> AdditiveLoft001
  Direction = (1,1,1)
  Length = 10
  Length2 = 100
  Profile = -> AdditiveLoft001 [Face45]
  Type = 0
  expr: Length = Spreadsheet.B15
FEATURE [Sketcher::SketchObject] Sketch021
  ExternalGeometry = -> [Pad007]
  FullyConstrained = true
  MapMode = 5
  Placement = pos=(0,13,0) rot=(0,0.707107,0.707107;3.14159rad)
  Support = -> [Pad007]
  sketch-geometry (9):
    g0: LineSegment StartX=-10.8 StartY=12.7 StartZ=0 EndX=-4.2 EndY=12.7 EndZ=0
    g1: LineSegment StartX=-4.2 StartY=12.7 StartZ=0 EndX=-4.2 EndY=9.2 EndZ=0
    g2: LineSegment StartX=-4.2 StartY=9.2 StartZ=0 EndX=-10.8 EndY=9.2 EndZ=0
    g3: LineSegment StartX=-10.8 StartY=9.2 StartZ=0 EndX=-10.8 EndY=12.7 EndZ=0
    g4: LineSegment StartX=-12.8 StartY=14.7 StartZ=0 EndX=-2.2 EndY=14.7 EndZ=0
    g5: LineSegment StartX=-2.2 StartY=14.7 StartZ=0 EndX=-2.2 EndY=7.2 EndZ=0
    g6: LineSegment StartX=-2.2 StartY=7.2 StartZ=0 EndX=-12.8 EndY=7.2 EndZ=0
    g7: LineSegment StartX=-12.8 StartY=7.2 StartZ=0 EndX=-12.8 EndY=14.7 EndZ=0
    g8: GeomPoint X=-7.5 Y=10.95 Z=0
  constraints (22):
    c: Coincident(g0,g1)
    c: Coincident(g1,g2)
    c: Coincident(g2,g3)
    c: Coincident(g3,g0)
    c: Horizontal(g0)
    c: Horizontal(g2)
    c: Vertical(g1)
    c: Vertical(g3)
    c: Coincident(g0,g-3)
    c: Coincident(g1,g-4)
    c: Coincident(g4,g5)
    c: Coincident(g5,g6)
    c: Coincident(g6,g7)
    c: Coincident(g7,g4)
    c: Horizontal(g4)
    c: Horizontal(g6)
    c: Vertical(g5)
    c: Vertical(g7)
    c: Symmetric(g0,g1,g8)
    c: Symmetric(g4,g5,g8)
    c: DistanceX(g4,g0) = 2
    c: DistanceY(g0,g4) = 2
FEATURE [Sketcher::SketchObject] Sketch022
  AttachmentOffset = pos=(0,0,9.5) rot=(0,0,1;0rad)
  ExternalGeometry = -> [Pad007]
  FullyConstrained = true
  MapMode = 5
  Placement = pos=(0,22.5,-2.1e-15) rot=(0,0.707107,0.707107;3.14159rad)
  Support = -> [Pad007]
  expr: .AttachmentOffset.Base.z = Spreadsheet.B14
  sketch-geometry (3):
    g0: Circle CenterX=-7.5 CenterY=9.175 CenterZ=0 NormalX=0 NormalY=0 NormalZ=1 AngleXU=0 Radius=4
    g1: Circle CenterX=-7.5 CenterY=9.175 CenterZ=0 NormalX=0 NormalY=0 NormalZ=1 AngleXU=0 Radius=6
    g2: GeomPoint X=-7.5 Y=12.7 Z=0
  constraints (6):
    c: Diameter(g0) = 8
    c: Coincident(g1,g0)
    c: Diameter(g1) = 12
    c: Symmetric(g-5,g-4,g2)
    c: Vertical(g2,g0)
    c: Horizontal(g0,g-3)
FEATURE [PartDesign::AdditiveLoft] AdditiveLoft002
  BaseFeature = -> Pad007
  Closed = false
  Profile = -> Sketch021
  Ruled = false
  Sections = -> [Sketch022]
FEATURE [PartDesign::Pad] Pad008
  BaseFeature = -> AdditiveLoft002
  Direction = (1,1,1)
  Length = 10
  Length2 = 100
  Profile = -> AdditiveLoft002 [Face49]
  Type = 0
  expr: Length = Spreadsheet.B15
FEATURE [PartDesign::Body] Body001  label="Mount V2"
  Group = -> [Sketch012,Pad004,Sketch013,Pocket006,Sketch014,Pocket007,Sketch015,Pocket008,Sketch016,Pad005,Sketch017,Pad006,Sketch018,Pocket009,Sketch020,Sketch019,AdditiveLoft001,Pad007,Sketch021,Sketch022,AdditiveLoft002,Pad008]
  Origin = -> Origin002
  Placement = pos=(35,146,0) rot=(0,0,1;0rad)
  Tip = -> Pad008
FEATURE [Part::Feature] Part__Feature012  label="1555FF42 BOX"
  Placement = pos=(86.47,161.265,41.95) rot=(0,0,-1;1.5708rad)
  shape: bbox 89.96 x 120 x 315.8 mm, 255 faces (baked)
FEATURE [App::Part] _555FF42  label="1555FF42"
  Group = -> [Part__Feature012]
  Origin = -> Origin003
FEATURE [PartDesign::ShapeBinder] ShapeBinder
  Placement = pos=(86.47,161.265,41.95) rot=(0,0,-1;1.5708rad)
  Support = -> [Part__Feature012]
  TraceSupport = false
FEATURE [PartDesign::ShapeBinder] ShapeBinder001
  Placement = pos=(35,146,0) rot=(0,0,1;0rad)
  Support = -> [Body001]
  TraceSupport = false
FEATURE [Sketcher::SketchObject] Sketch023
  ExternalGeometry = -> [ShapeBinder001,ShapeBinder]
  FullyConstrained = true
  MapMode = 5
  Placement = pos=(0,174,0) rot=(-1,0,0;4.71239rad)
  sketch-geometry (6):
    g0: LineSegment StartX=98.6621 StartY=44.45 StartZ=0 EndX=97.3659 EndY=-5.05 EndZ=0
    g1: LineSegment StartX=8.53118 StartY=44.45 StartZ=0 EndX=9.82738 EndY=-5.05 EndZ=0
    g2: LineSegment StartX=98.6621 StartY=44.45 StartZ=0 EndX=8.53118 EndY=44.45 EndZ=0
    g3: Circle CenterX=64.4 CenterY=9.175 CenterZ=0 NormalX=0 NormalY=0 NormalZ=1 AngleXU=0 Radius=6
    g4: Circle CenterX=42.5 CenterY=9.175 CenterZ=0 NormalX=0 NormalY=0 NormalZ=1 AngleXU=0 Radius=6
    g5: LineSegment StartX=97.3659 StartY=-5.05 StartZ=0 EndX=9.82738 EndY=-5.05 EndZ=0
  constraints (16):
    c: PointOnObject(g-5,g0)
    c: PointOnObject(g-5,g0)
    c: PointOnObject(g-6,g1)
    c: PointOnObject(g-6,g1)
    c: Coincident(g2,g0)
    c: Coincident(g2,g1)
    c: Coincident(g3,g-4)
    c: Coincident(g4,g-3)
    c: Coincident(g5,g0)
    c: Coincident(g5,g1)
    c: Horizontal(g-7,g1)
    c: Horizontal(g-7,g0)
    c: Horizontal(g2,g-8)
    c: Horizontal(g2,g-8)
    c: Equal(g-4,g4)
    c: Equal(g4,g3)
FEATURE [PartDesign::Pad] Pad009
  Direction = (1,1,1)
  Length = 2
  Length2 = 100
  Placement = pos=(0,174,0) rot=(-1,0,0;4.71239rad)
  Profile = -> Sketch023
  Reversed = true
  Type = 0
FEATURE [Sketcher::SketchObject] Sketch024
  ExternalGeometry = -> [Pad009]
  FullyConstrained = false
  MapMode = 5
  Placement = pos=(0,176,4e-16) rot=(-1,0,0;1.5708rad)
  Support = -> [Pad009]
  sketch-geometry (13):
    g0: LineSegment StartX=9.82738 StartY=5.05 StartZ=0 EndX=8.53118 EndY=-44.45 EndZ=0
    g1: LineSegment StartX=8.53118 StartY=-44.45 StartZ=0 EndX=98.6621 EndY=-44.45 EndZ=0
    g2: LineSegment StartX=98.6621 StartY=-44.45 StartZ=0 EndX=97.3659 EndY=5.05 EndZ=0
    g3: LineSegment StartX=97.3659 StartY=5.05 StartZ=0 EndX=9.82738 EndY=5.05 EndZ=0
    g4: LineSegment StartX=7.87907 StartY=7.05 StartZ=0 EndX=99.3142 EndY=7.05 EndZ=0
    g5: LineSegment StartX=99.3142 StartY=7.05 StartZ=0 EndX=100.715 EndY=-46.45 EndZ=0
    g6: LineSegment StartX=100.715 StartY=-46.45 StartZ=0 EndX=6.47812 EndY=-46.45 EndZ=0
    g7: LineSegment StartX=6.47812 StartY=-46.45 StartZ=0 EndX=7.87907 EndY=7.05 EndZ=0
    g8: GeomPoint X=54.2447 Y=-19.7 Z=0
    g9: LineSegment StartX=53.9452 StartY=7.05 StartZ=0 EndX=53.9452 EndY=5.05 EndZ=0
    g10: LineSegment StartX=69.1121 StartY=-44.45 StartZ=0 EndX=69.1121 EndY=-46.45 EndZ=0
    g11: LineSegment StartX=97.8043 StartY=-11.6903 StartZ=0 EndX=99.8036 EndY=-11.6379 EndZ=0
    g12: LineSegment StartX=9.34162 StartY=-13.5005 StartZ=0 EndX=7.3423 EndY=-13.4482 EndZ=0
  constraints (32):
    c: Coincident(g0,g-3)
    c: Coincident(g0,g-6)
    c: Coincident(g1,g0)
    c: Coincident(g1,g-5)
    c: Coincident(g2,g1)
    c: Coincident(g2,g-4)
    c: Coincident(g3,g2)
    c: Coincident(g3,g0)
    c: Coincident(g4,g5)
    c: Coincident(g5,g6)
    c: Coincident(g6,g7)
    c: Coincident(g7,g4)
    c: Parallel(g7,g0)
    c: Parallel(g5,g2)
    c: Parallel(g3,g4)
    c: Parallel(g1,g6)
    c: PointOnObject(g9,g4)
    c: PointOnObject(g9,g3)
    c: PointOnObject(g10,g1)
    c: PointOnObject(g10,g6)
    c: PointOnObject(g11,g2)
    c: PointOnObject(g11,g5)
    c: PointOnObject(g12,g0)
    c: PointOnObject(g12,g7)
    c: Perpendicular(g0,g12)
    c: Perpendicular(g3,g9)
    c: Perpendicular(g2,g11)
    c: Perpendicular(g1,g10)
    c: Equal(g12,g9)
    c: Equal(g9,g11)
    c: Equal(g11,g10)
    c: Distance(g12) = 2
FEATURE [PartDesign::Pad] Pad010
  BaseFeature = -> Pad009
  Direction = (1,1,1)
  Length = 30
  Length2 = 100
  Placement = pos=(0,174,0) rot=(-1,0,0;4.71239rad)
  Profile = -> Sketch024
  Reversed = true
  Type = 0
FEATURE [PartDesign::Body] Body002  label="Template001"
  Group = -> [ShapeBinder,ShapeBinder001,Sketch023,Pad009,Sketch024,Pad010]
  Origin = -> Origin004
  Tip = -> Pad010
